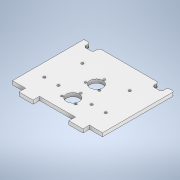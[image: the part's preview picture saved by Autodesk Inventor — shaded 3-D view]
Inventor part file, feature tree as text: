
AUTODESK INVENTOR PART (.ipt)
format: ipt  version: 2020 (Build 240168000, 168)  size: 220,160 bytes
history: native  units: mm
features: extrude x4, sketch x4, pattern_linear x3
ambient origin geometry x8: Origin, YZ Plane, XZ Plane, XY Plane, X Axis, Y Axis, Z Axis, Center Point
bodies: Solid1 (feature_tree)
feature tree (11):
  extrude  "base"  Depth=3.0mm
  extrude  "Poke Hole"  Depth=3.0mm
  pattern_linear  "Rectangular Pattern1"  Spacing1=9.0mm  [1 undecoded]
  extrude  "Mount Holes"  Depth=19.7mm
  pattern_linear  "Rectangular Pattern2"  Spacing1=1.5mm  [1 undecoded]
  extrude  "PCB mount holes"  Depth=126.0mm
  pattern_linear  "Rectangular Pattern3"  Spacing1=18.25mm  [1 undecoded]
  sketch  "Sketch1"  dims[d3=12.7mm d5=3.0mm]
  sketch  "Sketch2"  dims[d7=12.7mm d9=3.0mm]
  sketch  "Sketch3"  dims[d10=9.0mm]
  sketch  "Sketch4"  dims[d11=19.7mm d13=9.0mm d14=19.7mm d16=1.5mm d17=126.0mm d20=18.25mm d21=18.25mm d22=57.15mm d23=9.0mm d24=9.0mm d27=91.0mm d28=91.0mm d29=5.0mm d30=0.0mm d31=18.0mm d32=21.5mm d33=5.0mm d34=0.0mm d35=20.0mm d37=33.0mm d38=10.0mm d40=33.0mm d41=3.0mm d42=11.1mm d43=30.0mm d45=360.0deg d47=5.0mm d48=0.0mm d49=20.0mm d51=33.0mm d52=33.0mm d53=83.0mm d54=3.7mm d55=3.3mm d56=3.3mm d57=19.75mm d58=3.3mm d59=44.5mm d62=10.0mm d63=0.0mm d64=20.0mm d66=66.0mm]
note: 3 required parameter values undecoded (feature->parameter linkage not recoverable at this tier; creation-order binding heuristic only, values carry confidence <= 0.55)
